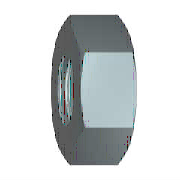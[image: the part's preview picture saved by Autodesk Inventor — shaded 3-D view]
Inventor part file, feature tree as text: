
AUTODESK INVENTOR PART (.ipt)
format: ipt  version: 2018 (Build 220112000, 112)  size: 175,104 bytes
history: native  units: mm (DEFAULTED — no unit token found)
features: sketch x3, chamfer x1, hole x1, other x1, plane x1
ambient origin geometry x7: Origin, YZ Plane, XZ Plane, X Axis, Y Axis, Z Axis, Center Point
bodies: Solid1 (feature_tree), Body (feature_tree)
feature tree (7):
  chamfer  "Chamfer1"  Angle=30.0deg  [1 undecoded]
  hole  "Thread"  [1 undecoded]
  other  "Work Axis1"
  plane  "Work Plane1"
  sketch  "Sketch1"  dims[d0=6.350853mm]
  sketch  "Sketch2"  dims[d1=2.9mm]
  sketch  "Sketch3"  dims[d2=0.0mm d3=30.0deg d4=30.0deg d5=5.5mm d6=5.5mm d7=90.0deg d25=2.459mm d26=6.0mm d27=4.0mm d28=2.0mm d29=14.3117mm d30=8.0mm d31=20.594885mm d8=0.270633mm d9=30.0deg d10=0.270633mm d11=30.0deg d13=0.0mm d14=0.0mm d39=0.0mm d40=0.270633mm d41=0.270633mm d42=0.0mm]
note: 2 required parameter values undecoded (feature->parameter linkage not recoverable at this tier; creation-order binding heuristic only, values carry confidence <= 0.55)
